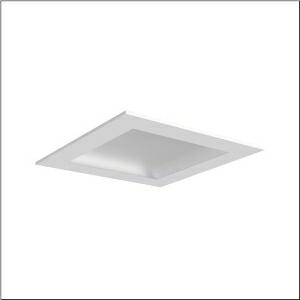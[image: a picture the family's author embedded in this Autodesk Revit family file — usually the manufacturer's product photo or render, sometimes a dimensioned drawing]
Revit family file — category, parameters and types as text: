
# Revit family: mira_11_sl_51fr427a433a
name_source: partatom
category: Lighting Fixtures
units: mm (PartAtom-declared; Revit-internal decimal feet)

## family parameters
Cut with Voids When Loaded = No
Host = Face
Light Source = No
Part Type = Normal
Room Calculation Point = No
Round Connector Dimension = Use Diameter
Shared = No

## types (1)
- Mira 11 SL (1 x LED, 3150 lm, 28 W, 4000K)
    Apparent Load = 28 VA
    CIE Flux Codes = 50 81 97 100 100
    Color Rendering = 80
    Color Temperature = 4000K
    Default Elevation = 1800 mm
    Description = Mira 11 SL, clean room luminaire, primary light control with reflector, primary optical cover: cover, of PC, light emission: direct distribution, primary light characteristic: symmetric, installation type: recessed, LED, rated luminous flux: 3.150lm, luminous efficacy: 113lm/W, light colour: 840, colour temperature: 4000K, control gear: ON/OFF, with terminal, 3-pole, max. 2.5mm², mains connection: 230V, AC, 50/60Hz, rated input power: 28W, luminaire housing, of sheet steel, coated, pure white (RAL 9010), with wing nuts, module: M625, length: 623mm, width: 623mm, height: 91mm, protection rating (complete): IP54, protection rating (on room side): IP65, insulation class (complete): insulation class I (protective earthing), certification: CE, UKCA, permissible operating ambient temperature: -5..+40°C, standard: EN 50419, packaging unit: 1 piece
    Height = 0 mm  [stored 0 ft]
    Lamp = 1 x LED
    Lamp Light Flux = 3150 lm
    Lamp Power = 28 W
    Lamp count = 1
    Length = 625 mm
    Luminous efficacy = 113 lm/W
    Manufacturer = Siteco
    ModVariant = No
    Model = 51FR427A433A
    Mounting Place = Ceiling
    Mounting Type = Recessed
    Number of Poles = 1
    OnlyDefault = Yes
    Power Factor = 1
    Product Name = Mira 11 SL
    Product group = clean room luminaire | ceiling recessed
    ProductGroupID = 402
    Protection Class = Protection class I
    Protection Degree = IP 54
    RLX_Detail_Level = 1
    RLX_Emergency_Light_Flux = 0 lm
    RLX_Emergency_Type = 0
    RLX_Emergency_Type_DB = No
    RlxData = <blob elided: 19941 chars, md5=13c52daf>
    Socket = socket
    Standby Power = 0 W
    System Light Flux = 3150 lm
    System Power = 28 W
    Type Comments = Product without accessories
    Type Image = l_1007111.jpg
    URL = http://relux.com
    VarID = ---
    Voltage = 0 V
    Weight = 0.00 kg
    Width = 625 mm

note: [stored X ft] marks values corroborated as IEEE doubles in the binary element streams (Revit-internal decimal feet)

## geometry (parser evidence)
native form markers: Blend x4, Sweep x12
no freeform markers — native parametric forms only
